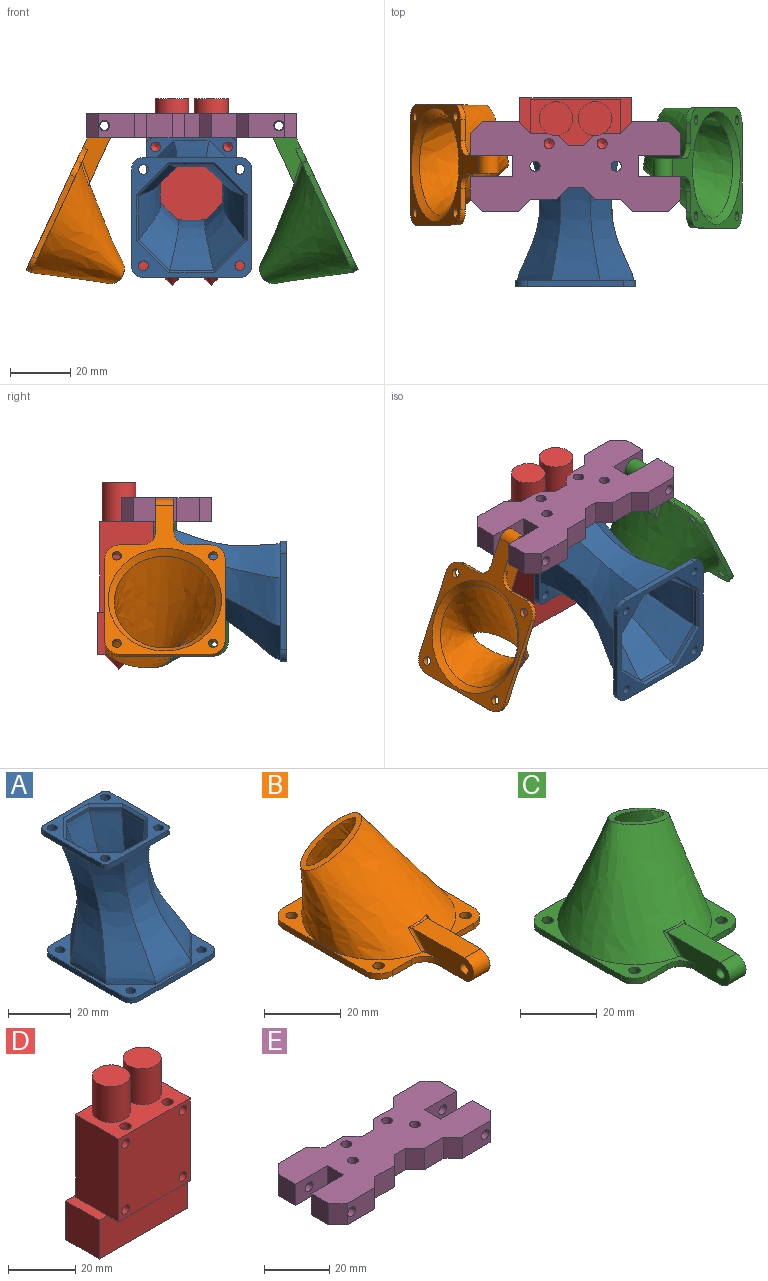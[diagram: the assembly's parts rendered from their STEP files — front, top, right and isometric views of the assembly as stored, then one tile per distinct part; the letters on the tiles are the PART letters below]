
ASSEMBLY  parts=5 mates=4
PART A: 76 faces, bbox 40x46.5x44 mm
  f0: bspline ~40x24.82mm, area 511.6mm2, adj f1,f7,f16,f30
  f1: bspline ~40x25.33mm, area 484mm2, adj f0,f2,f16,f30
  f2: bspline ~40x17.75mm, area 474.6mm2, adj f1,f3,f16,f30
  f3: bspline ~40x15.91mm, area 476.6mm2, adj f2,f4,f16,f30
  f4: bspline ~40x17.75mm, area 474.6mm2, adj f3,f5,f16,f30
  f5: bspline ~40x25.33mm, area 484mm2, adj f4,f6,f16,f30
  f6: bspline ~40x24.82mm, area 511.6mm2, adj f5,f7,f16,f30
  f7: bspline ~40x19.72mm, area 527.6mm2, adj f0,f6,f16,f30
  f8: bspline ~40x23.88mm, area 450.8mm2, adj f9,f15,f23,f40
  f9: bspline ~40x19.72mm, area 465mm2, adj f8,f10,f24,f39
  f10: bspline ~40x23.88mm, area 450.8mm2, adj f9,f11,f25,f38
  f11: bspline ~40x24.01mm, area 426.4mm2, adj f10,f12,f26,f37
  f12: bspline ~40x16.81mm, area 418mm2, adj f11,f13,f27,f36
  f13: bspline ~40x14.58mm, area 419.7mm2, adj f12,f14,f28,f43
  f14: bspline ~40x16.81mm, area 418mm2, adj f13,f15,f29,f42
  f15: bspline ~40x24.01mm, area 426.4mm2, adj f8,f14,f22,f41
  f16: plane 40x40mm, normal (0,0,1), area 332.5mm2, adj f0,f1,f2,f3,f4,f5,f6,f7
  f17: plane 32x2mm, normal (-1,0,0), area 64mm2, adj f16,f21,f56,f59
  f18: plane 32x2mm, normal (0,-1,0), area 64mm2, adj f16,f21,f56,f57
  f19: plane 32x2mm, normal (1,0,0), area 64mm2, adj f16,f21,f57,f58
  f20: plane 32x2mm, normal (0,1,0), area 64mm2, adj f16,f21,f58,f59
  f21: plane 40x40mm, normal (0,0,-1), area 432.2mm2, adj f17,f18,f19,f20,f48,f49,f50,f51
  f22: plane 14.58x1.2mm, normal (1,0,0), area 17.5mm2, adj f15,f23,f29,f74
  f23: plane 10.31x10.31mm, normal (0.71,0.71,0), area 17.5mm2, adj f8,f22,f24,f72
  f24: plane 14.58x1.2mm, normal (0,1,0), area 17.5mm2, adj f9,f23,f25,f70
  f25: plane 10.31x10.31mm, normal (-0.71,0.71,0), area 17.5mm2, adj f10,f24,f26,f68
  f26: plane 14.58x1.2mm, normal (-1,0,0), area 17.5mm2, adj f11,f25,f27,f69
  f27: plane 10.31x10.31mm, normal (-0.71,-0.71,0), area 17.5mm2, adj f12,f26,f28,f71
  f28: plane 14.58x1.2mm, normal (0,-1,0), area 17.5mm2, adj f13,f27,f29,f73
  f29: plane 10.31x10.31mm, normal (0.71,-0.71,0), area 17.5mm2, adj f14,f22,f28,f75
  f30: plane 30x30mm, normal (0,0,-1), area 196.2mm2, adj f0,f1,f2,f3,f4,f5,f6,f7
  f31: plane 26x2mm, normal (0,-1,0), area 52mm2, adj f30,f35,f52,f55
  f32: plane 26x2mm, normal (1,0,0), area 52mm2, adj f30,f35,f52,f53
  f33: plane 26x2mm, normal (0,1,0), area 52mm2, adj f30,f35,f53,f54
  f34: plane 26x2mm, normal (-1,0,0), area 52mm2, adj f30,f35,f54,f55
  f35: plane 30x30mm, normal (0,0,1), area 269.4mm2, adj f31,f32,f33,f34,f44,f45,f46,f47
  f36: plane 7.38x7.38mm, normal (-0.71,-0.71,0), area 12.5mm2, adj f12,f37,f43,f67
  f37: plane 10.44x1.2mm, normal (-1,0,0), area 12.5mm2, adj f11,f36,f38,f65
  f38: plane 7.38x7.38mm, normal (-0.71,0.71,0), area 12.5mm2, adj f10,f37,f39,f63
  f39: plane 10.44x1.2mm, normal (0,1,0), area 12.5mm2, adj f9,f38,f40,f61
  f40: plane 7.38x7.38mm, normal (0.71,0.71,0), area 12.5mm2, adj f8,f39,f41,f60
  f41: plane 10.44x1.2mm, normal (1,0,0), area 12.5mm2, adj f15,f40,f42,f62
  f42: plane 7.38x7.38mm, normal (0.71,-0.71,0), area 12.5mm2, adj f14,f41,f43,f64
  f43: plane 10.44x1.2mm, normal (0,-1,0), area 12.5mm2, adj f13,f36,f42,f66
  f44: cylinder r=1.6mm len=3.2mm, axis (0,0,-1), area 20.1mm2, adj f30,f35
  f45: cylinder r=1.6mm len=3.2mm, axis (0,0,-1), area 20.1mm2, adj f30,f35
  f46: cylinder r=1.6mm len=3.2mm, axis (0,0,-1), area 20.1mm2, adj f30,f35
  f47: cylinder r=1.6mm len=3.2mm, axis (0,0,-1), area 20.1mm2, adj f30,f35
  f48: cylinder r=1.6mm len=3.2mm, axis (0,0,1), area 20.1mm2, adj f16,f21
  f49: cylinder r=1.6mm len=3.2mm, axis (0,0,1), area 20.1mm2, adj f16,f21
  f50: cylinder r=1.6mm len=3.2mm, axis (0,0,1), area 20.1mm2, adj f16,f21
  f51: cylinder r=1.6mm len=3.2mm, axis (0,0,1), area 20.1mm2, adj f16,f21
  f52: cylinder r=2mm len=2mm, axis (0,0,1), area 6.3mm2, adj f30,f31,f32,f35
  f53: cylinder r=2mm len=2mm, axis (0,0,-1), area 6.3mm2, adj f30,f32,f33,f35
  f54: cylinder r=2mm len=2mm, axis (0,0,1), area 6.3mm2, adj f30,f33,f34,f35
  f55: cylinder r=2mm len=2mm, axis (0,0,-1), area 6.3mm2, adj f30,f31,f34,f35
  f56: cylinder r=4mm len=4mm, axis (0,0,-1), area 12.6mm2, adj f16,f17,f18,f21
  f57: cylinder r=4mm len=4mm, axis (0,0,1), area 12.6mm2, adj f16,f18,f19,f21
  f58: cylinder r=4mm len=4mm, axis (0,0,-1), area 12.6mm2, adj f16,f19,f20,f21
  f59: cylinder r=4mm len=4mm, axis (0,0,1), area 12.6mm2, adj f16,f17,f20,f21
  f60: plane 8.18x8.18mm, normal (0.5,0.5,0.71), area 12.2mm2, adj f35,f40,f61,f62
  f61: plane 11.1x0.8mm, normal (0,0.71,0.71), area 12.2mm2, adj f35,f39,f60,f63
  f62: plane 11.1x0.8mm, normal (0.71,0,0.71), area 12.2mm2, adj f35,f41,f60,f64
  f63: plane 8.18x8.18mm, normal (-0.5,0.5,0.71), area 12.2mm2, adj f35,f38,f61,f65
  f64: plane 8.18x8.18mm, normal (0.5,-0.5,0.71), area 12.2mm2, adj f35,f42,f62,f66
  f65: plane 11.1x0.8mm, normal (-0.71,0,0.71), area 12.2mm2, adj f35,f37,f63,f67
  f66: plane 11.1x0.8mm, normal (0,-0.71,0.71), area 12.2mm2, adj f35,f43,f64,f67
  f67: plane 8.18x8.18mm, normal (-0.5,-0.5,0.71), area 12.2mm2, adj f35,f36,f65,f66
  f68: plane 11.11x11.11mm, normal (-0.5,0.5,-0.71), area 16.9mm2, adj f21,f25,f69,f70
  f69: plane 15.24x0.8mm, normal (-0.71,0,-0.71), area 16.9mm2, adj f21,f26,f68,f71
  f70: plane 15.24x0.8mm, normal (0,0.71,-0.71), area 16.9mm2, adj f21,f24,f68,f72
  f71: plane 11.11x11.11mm, normal (-0.5,-0.5,-0.71), area 16.9mm2, adj f21,f27,f69,f73
  f72: plane 11.11x11.11mm, normal (0.5,0.5,-0.71), area 16.9mm2, adj f21,f23,f70,f74
  f73: plane 15.24x0.8mm, normal (0,-0.71,-0.71), area 16.9mm2, adj f21,f28,f71,f75
  f74: plane 15.24x0.8mm, normal (0.71,0,-0.71), area 16.9mm2, adj f21,f22,f72,f75
  f75: plane 11.11x11.11mm, normal (0.5,-0.5,-0.71), area 16.9mm2, adj f21,f29,f73,f74
PART B: 32 faces, bbox 40.2x58.2x31.4 mm
  f0: plane 20.75x9.07mm, normal (-0.34,0,0.94), area 70.3mm2, adj f3,f31
  f1: plane 7x1.8mm, normal (0,-1,0), area 12.6mm2, adj f4,f11,f17,f26
  f2: plane 25.22x17.22mm, normal (0,0,1), area 78.4mm2, adj f3,f9,f10,f13,f18,f23,f27,f28
  f3: bspline ~39.97x39.96mm, area 2468.1mm2, adj f0,f2,f4,f5,f6,f28,f29,f30
  f4: plane 25.22x17.22mm, normal (0,0,1), area 78.4mm2, adj f1,f3,f8,f12,f17,f21,f26,f30
  f5: plane 20.07x20.07mm, normal (0,0,1), area 73.4mm2, adj f3,f7,f8,f15,f16
  f6: plane 20.07x20.07mm, normal (0,0,1), area 73.4mm2, adj f3,f7,f10,f14,f19
  f7: plane 30x1.8mm, normal (0,1,0), area 54mm2, adj f5,f6,f11,f16,f19
  f8: plane 30x1.8mm, normal (-1,0,0), area 54mm2, adj f4,f5,f11,f16,f17
  f9: plane 7x1.8mm, normal (0,-1,0), area 12.6mm2, adj f2,f11,f18,f27
  f10: plane 30x1.8mm, normal (1,0,0), area 54mm2, adj f2,f6,f11,f18,f19
  f11: plane 54.5x40mm, normal (0,0,-1), area 537.6mm2, adj f1,f7,f8,f9,f10,f12,f13,f14
  f12: cylinder r=1.5mm len=3mm, axis (0,0,-1), area 17mm2, adj f4,f11
  f13: cylinder r=1.5mm len=3mm, axis (0,0,-1), area 17mm2, adj f2,f11
  f14: cylinder r=1.5mm len=3mm, axis (0,0,-1), area 17mm2, adj f6,f11
  f15: cylinder r=1.5mm len=3mm, axis (0,0,-1), area 17mm2, adj f5,f11
  f16: cylinder r=5mm len=5mm, axis (0,0,-1), area 14.1mm2, adj f5,f7,f8,f11
  f17: cylinder r=5mm len=5mm, axis (0,0,1), area 14.1mm2, adj f1,f4,f8,f11
  f18: cylinder r=5mm len=5mm, axis (0,0,-1), area 14.1mm2, adj f2,f9,f10,f11
  f19: cylinder r=5mm len=5mm, axis (0,0,1), area 14.1mm2, adj f6,f7,f10,f11
  f20: cone r=16.8mm half-angle=45deg, axis (0,0,-1), area 316.3mm2, adj f11,f31
  f21: plane 22.1x7mm, normal (-1,0,0), area 113.4mm2, adj f4,f11,f22,f24,f25,f26,f30
  f22: plane 19.72x6.34mm, normal (0,0,1), area 115.9mm2, adj f21,f23,f24,f28,f29,f30
  f23: plane 22.54x7mm, normal (1,0,0), area 114.4mm2, adj f2,f11,f22,f24,f25,f27,f28
  f24: cylinder r=3.5mm len=7mm, axis (-1,0,0), area 66mm2, adj f11,f21,f22,f23
  f25: cylinder r=1.5mm len=6mm, axis (-1,0,0), area 56.5mm2, adj f21,f23
  f26: cylinder r=5mm len=5mm, axis (0,0,-1), area 14.1mm2, adj f1,f4,f11,f21
  f27: cylinder r=5mm len=5mm, axis (0,0,1), area 14.1mm2, adj f2,f9,f11,f23
  f28: bspline ~11.87x11.63mm, area 8.6mm2, adj f2,f3,f22,f23,f29
  f29: bspline ~9.39x1.4mm, area 4.4mm2, adj f3,f22,f28,f30
  f30: bspline ~9.86x9.25mm, area 8.5mm2, adj f3,f4,f21,f22,f29
  f31: bspline ~35.11x33.58mm, area 2025.1mm2, adj f0,f20
PART C: 32 faces, bbox 40.2x58.2x31.4 mm
  f0: plane 20.75x9.07mm, normal (0.34,0,0.94), area 70.2mm2, adj f3,f31
  f1: plane 7x1.8mm, normal (0,-1,0), area 12.6mm2, adj f4,f11,f17,f26
  f2: plane 25.22x17.22mm, normal (0,0,1), area 78.4mm2, adj f3,f9,f10,f13,f18,f23,f27,f28
  f3: bspline ~39.97x39.96mm, area 2468.1mm2, adj f0,f2,f4,f5,f6,f28,f29,f30
  f4: plane 25.22x17.22mm, normal (0,0,1), area 78.4mm2, adj f1,f3,f8,f12,f17,f21,f26,f30
  f5: plane 20.07x20.07mm, normal (0,0,1), area 73.4mm2, adj f3,f7,f8,f15,f16
  f6: plane 20.07x20.07mm, normal (0,0,1), area 73.4mm2, adj f3,f7,f10,f14,f19
  f7: plane 30x1.8mm, normal (0,1,0), area 54mm2, adj f5,f6,f11,f16,f19
  f8: plane 30x1.8mm, normal (-1,0,0), area 54mm2, adj f4,f5,f11,f16,f17
  f9: plane 7x1.8mm, normal (0,-1,0), area 12.6mm2, adj f2,f11,f18,f27
  f10: plane 30x1.8mm, normal (1,0,0), area 54mm2, adj f2,f6,f11,f18,f19
  f11: plane 54.5x40mm, normal (0,0,-1), area 537.6mm2, adj f1,f7,f8,f9,f10,f12,f13,f14
  f12: cylinder r=1.5mm len=3mm, axis (0,0,-1), area 17mm2, adj f4,f11
  f13: cylinder r=1.5mm len=3mm, axis (0,0,-1), area 17mm2, adj f2,f11
  f14: cylinder r=1.5mm len=3mm, axis (0,0,-1), area 17mm2, adj f6,f11
  f15: cylinder r=1.5mm len=3mm, axis (0,0,-1), area 17mm2, adj f5,f11
  f16: cylinder r=5mm len=5mm, axis (0,0,-1), area 14.1mm2, adj f5,f7,f8,f11
  f17: cylinder r=5mm len=5mm, axis (0,0,1), area 14.1mm2, adj f1,f4,f8,f11
  f18: cylinder r=5mm len=5mm, axis (0,0,-1), area 14.1mm2, adj f2,f9,f10,f11
  f19: cylinder r=5mm len=5mm, axis (0,0,1), area 14.1mm2, adj f6,f7,f10,f11
  f20: cone r=16.8mm half-angle=45deg, axis (0,0,-1), area 316.3mm2, adj f11,f31
  f21: plane 22.54x7mm, normal (-1,0,0), area 114.4mm2, adj f4,f11,f22,f24,f25,f26,f30
  f22: plane 19.72x6.35mm, normal (0,0,1), area 115.9mm2, adj f21,f23,f24,f28,f29,f30
  f23: plane 22.1x7mm, normal (1,0,0), area 113.4mm2, adj f2,f11,f22,f24,f25,f27,f28
  f24: cylinder r=3.5mm len=7mm, axis (-1,0,0), area 66mm2, adj f11,f21,f22,f23
  f25: cylinder r=1.5mm len=6mm, axis (-1,0,0), area 56.5mm2, adj f21,f23
  f26: cylinder r=5mm len=5mm, axis (0,0,-1), area 14.1mm2, adj f1,f4,f11,f21
  f27: cylinder r=5mm len=5mm, axis (0,0,1), area 14.1mm2, adj f2,f9,f11,f23
  f28: bspline ~9.86x9.25mm, area 8.5mm2, adj f2,f3,f22,f23,f29
  f29: bspline ~9.8x1.54mm, area 4.4mm2, adj f3,f22,f28,f30
  f30: bspline ~11.87x11.63mm, area 8.6mm2, adj f3,f4,f21,f22,f29
  f31: bspline ~35.15x33.58mm, area 2021.9mm2, adj f0,f20
PART D: 30 faces, bbox 37x18.6x62 mm
  f0: plane 30x4.6mm, normal (0,0,-1), area 138mm2, adj f3,f4,f6,f24
  f1: cylinder r=1.7mm len=9mm, axis (0,0,1), area 95.1mm2, adj f7,f13,f17
  f2: cylinder r=1.7mm len=9mm, axis (0,0,1), area 95.1mm2, adj f7,f12,f15
  f3: plane 30x30mm, normal (0,-1,0), area 867.8mm2, adj f0,f4,f6,f7,f15,f17,f19,f21
  f4: plane 30x18mm, normal (1,0,0), area 540mm2, adj f0,f3,f5,f7,f22
  f5: plane 30x30mm, normal (0,1,0), area 900mm2, adj f4,f6,f7,f22
  f6: plane 30x18mm, normal (-1,0,0), area 540mm2, adj f0,f3,f5,f7,f22
  f7: plane 30x18mm, normal (0,0,1), area 324.8mm2, adj f1,f2,f3,f4,f5,f6,f8,f10
  f8: cylinder r=5.6mm len=13mm, axis (0,0,-1), area 457.4mm2, adj f7,f9
  f9: plane 11.2x11.2mm, normal (0,0,1), area 98.5mm2, adj f8
  f10: cylinder r=5.6mm len=13mm, axis (0,0,-1), area 457.4mm2, adj f7,f11
  f11: plane 11.2x11.2mm, normal (0,0,1), area 98.5mm2, adj f10
  f12: cone r=0mm half-angle=59deg, axis (0,0,1), area 10.6mm2, adj f2
  f13: cone r=0mm half-angle=59deg, axis (0,0,1), area 10.6mm2, adj f1
  f14: cone r=0mm half-angle=59deg, axis (0,-1,0), area 9.4mm2, adj f15
  f15: cylinder r=1.6mm len=5mm, axis (0,-1,0), area 49.2mm2, adj f2,f3,f14
  f16: cone r=0mm half-angle=59deg, axis (0,-1,0), area 9.4mm2, adj f17
  f17: cylinder r=1.6mm len=5mm, axis (0,-1,0), area 49.2mm2, adj f1,f3,f16
  f18: cone r=0mm half-angle=59deg, axis (0,-1,0), area 9.4mm2, adj f19
  f19: cylinder r=1.6mm len=5mm, axis (0,-1,0), area 50.3mm2, adj f3,f18
  f20: cone r=0mm half-angle=59deg, axis (0,-1,0), area 9.4mm2, adj f21
  f21: cylinder r=1.6mm len=5mm, axis (0,-1,0), area 50.3mm2, adj f3,f20
  f22: plane 37x14mm, normal (0,0,1), area 116mm2, adj f4,f5,f6,f23,f24,f25,f26
  f23: plane 14x14mm, normal (1,0,0), area 196mm2, adj f22,f24,f26,f27
  f24: plane 37x14mm, normal (0,-1,0), area 518mm2, adj f0,f22,f23,f25,f27
  f25: plane 14x14mm, normal (-1,0,0), area 196mm2, adj f22,f24,f26,f27
  f26: plane 37x14mm, normal (0,1,0), area 518mm2, adj f22,f23,f25,f27
  f27: plane 37x14mm, normal (0,0,-1), area 360.9mm2, adj f23,f24,f25,f26,f28,f29
  f28: cone r=5mm half-angle=45deg, axis (0,0,1), area 111.1mm2, adj f27
  f29: cone r=5mm half-angle=45deg, axis (0,0,1), area 111.1mm2, adj f27
PART E: 46 faces, bbox 70x30x8 mm
  f0: plane 12x8mm, normal (0,-1,0), area 86.9mm2, adj f2,f15,f17,f39,f41
  f1: plane 12x8mm, normal (0,1,0), area 86.9mm2, adj f2,f15,f16,f42,f45
  f2: plane 70x30mm, normal (0,0,1), area 1491.7mm2, adj f0,f1,f3,f4,f5,f6,f7,f8
  f3: plane 14x8mm, normal (0,1,0), area 102.9mm2, adj f2,f4,f14,f15,f17
  f4: plane 8x7.5mm, normal (-1,0,0), area 60mm2, adj f2,f3,f15,f41
  f5: plane 12x8mm, normal (0,-1,0), area 86.9mm2, adj f2,f15,f19,f38,f40
  f6: plane 8x7.5mm, normal (1,0,0), area 60mm2, adj f2,f7,f15,f40
  f7: plane 14x8mm, normal (0,1,0), area 102.9mm2, adj f2,f6,f8,f15,f19
  f8: plane 8x7mm, normal (1,0,0), area 56mm2, adj f2,f7,f9,f15
  f9: plane 14x8mm, normal (0,-1,0), area 102.9mm2, adj f2,f8,f10,f15,f18
  f10: plane 8x7.5mm, normal (1,0,0), area 60mm2, adj f2,f9,f15,f43
  f11: plane 12x8mm, normal (0,1,0), area 86.9mm2, adj f2,f15,f18,f43,f44
  f12: plane 8x7.5mm, normal (-1,0,0), area 60mm2, adj f2,f13,f15,f42
  f13: plane 14x8mm, normal (0,-1,0), area 102.9mm2, adj f2,f12,f14,f15,f16
  f14: plane 8x7mm, normal (-1,0,0), area 56mm2, adj f2,f3,f13,f15
  f15: plane 70x30mm, normal (0,0,-1), area 1443.5mm2, adj f0,f1,f3,f4,f5,f6,f7,f8
  f16: cylinder r=1.7mm len=11.5mm, axis (0,-1,0), area 122.8mm2, adj f1,f13
  f17: cylinder r=1.7mm len=11.5mm, axis (0,-1,0), area 122.8mm2, adj f0,f3
  f18: cylinder r=1.7mm len=11.5mm, axis (0,-1,0), area 122.8mm2, adj f9,f11
  f19: cylinder r=1.7mm len=11.5mm, axis (0,-1,0), area 122.8mm2, adj f5,f7
  f20: cylinder r=1.7mm len=4.8mm, axis (0,0,-1), area 51.3mm2, adj f2,f21
  f21: plane 6.5x6.5mm, normal (0,0,-1), area 24.1mm2, adj f20,f22
  f22: cylinder r=3.25mm len=6.5mm, axis (0,0,-1), area 65.3mm2, adj f15,f21
  f23: cylinder r=1.7mm len=4.8mm, axis (0,0,-1), area 51.3mm2, adj f2,f24
  f24: plane 6.5x6.5mm, normal (0,0,-1), area 24.1mm2, adj f23,f25
  f25: cylinder r=3.25mm len=6.5mm, axis (0,0,-1), area 65.3mm2, adj f15,f24
  f26: cylinder r=1.7mm len=8mm, axis (0,0,1), area 85.5mm2, adj f2,f15
  f27: cylinder r=1.7mm len=8mm, axis (0,0,1), area 85.5mm2, adj f2,f15
  f28: plane 8.5x8mm, normal (0,-1,0), area 68mm2, adj f2,f15,f35,f38
  f29: plane 8x5mm, normal (0,-1,0), area 40mm2, adj f2,f15,f34,f35
  f30: plane 8.5x8mm, normal (0,-1,0), area 68mm2, adj f2,f15,f34,f39
  f31: plane 8.5x8mm, normal (0,1,0), area 68mm2, adj f2,f15,f37,f45
  f32: plane 8x5mm, normal (0,1,0), area 40mm2, adj f2,f15,f36,f37
  f33: plane 8.5x8mm, normal (0,1,0), area 68mm2, adj f2,f15,f36,f44
  f34: plane 8x4mm, normal (0.71,-0.71,0), area 45.3mm2, adj f2,f15,f29,f30
  f35: plane 8x4mm, normal (-0.71,-0.71,0), area 45.3mm2, adj f2,f15,f28,f29
  f36: plane 8x4mm, normal (-0.71,0.71,0), area 45.3mm2, adj f2,f15,f32,f33
  f37: plane 8x4mm, normal (0.71,0.71,0), area 45.3mm2, adj f2,f15,f31,f32
  f38: plane 8x4mm, normal (-0.71,-0.71,0), area 45.3mm2, adj f2,f5,f15,f28
  f39: plane 8x4mm, normal (0.71,-0.71,0), area 45.3mm2, adj f0,f2,f15,f30
  f40: plane 8x4mm, normal (0.71,-0.71,0), area 45.3mm2, adj f2,f5,f6,f15
  f41: plane 8x4mm, normal (-0.71,-0.71,0), area 45.3mm2, adj f0,f2,f4,f15
  f42: plane 8x4mm, normal (-0.71,0.71,0), area 45.3mm2, adj f1,f2,f12,f15
  f43: plane 8x4mm, normal (0.71,0.71,0), area 45.3mm2, adj f2,f10,f11,f15
  f44: plane 8x4mm, normal (-0.71,0.71,0), area 45.3mm2, adj f2,f11,f15,f33
  f45: plane 8x4mm, normal (0.71,0.71,0), area 45.3mm2, adj f1,f2,f15,f31
PLACE A rot(axis=(0,0.71,0.71),180deg) t=(-9.81,-49.29,21.03)mm
PLACE B rot(axis=(-0.64,0.64,-0.41),135.2deg) t=(-56.46,-10.99,21.69)mm
PLACE C rot(axis=(-0.64,-0.64,0.41),135.4deg) t=(36.99,-11.99,21.78)mm
PLACE D t=(-9.81,1.71,17.53)mm fixed
PLACE E t=(-9.81,-11.49,47.53)mm
MATE revolute C.f24 <-> E.f18  axis (0,-1,0) through (19.19,-14.99,51.53)mm
MATE fastened A.f47 <-> D.f16  axis (0,1,0) through (2.19,-7.29,44.53)mm
MATE revolute B.f24 <-> E.f16  axis (0,1,0) through (-38.81,-7.99,51.53)mm
MATE fastened E.f27 <-> D.f1  axis (0,0,-1) through (-1.01,-3.99,47.53)mm
